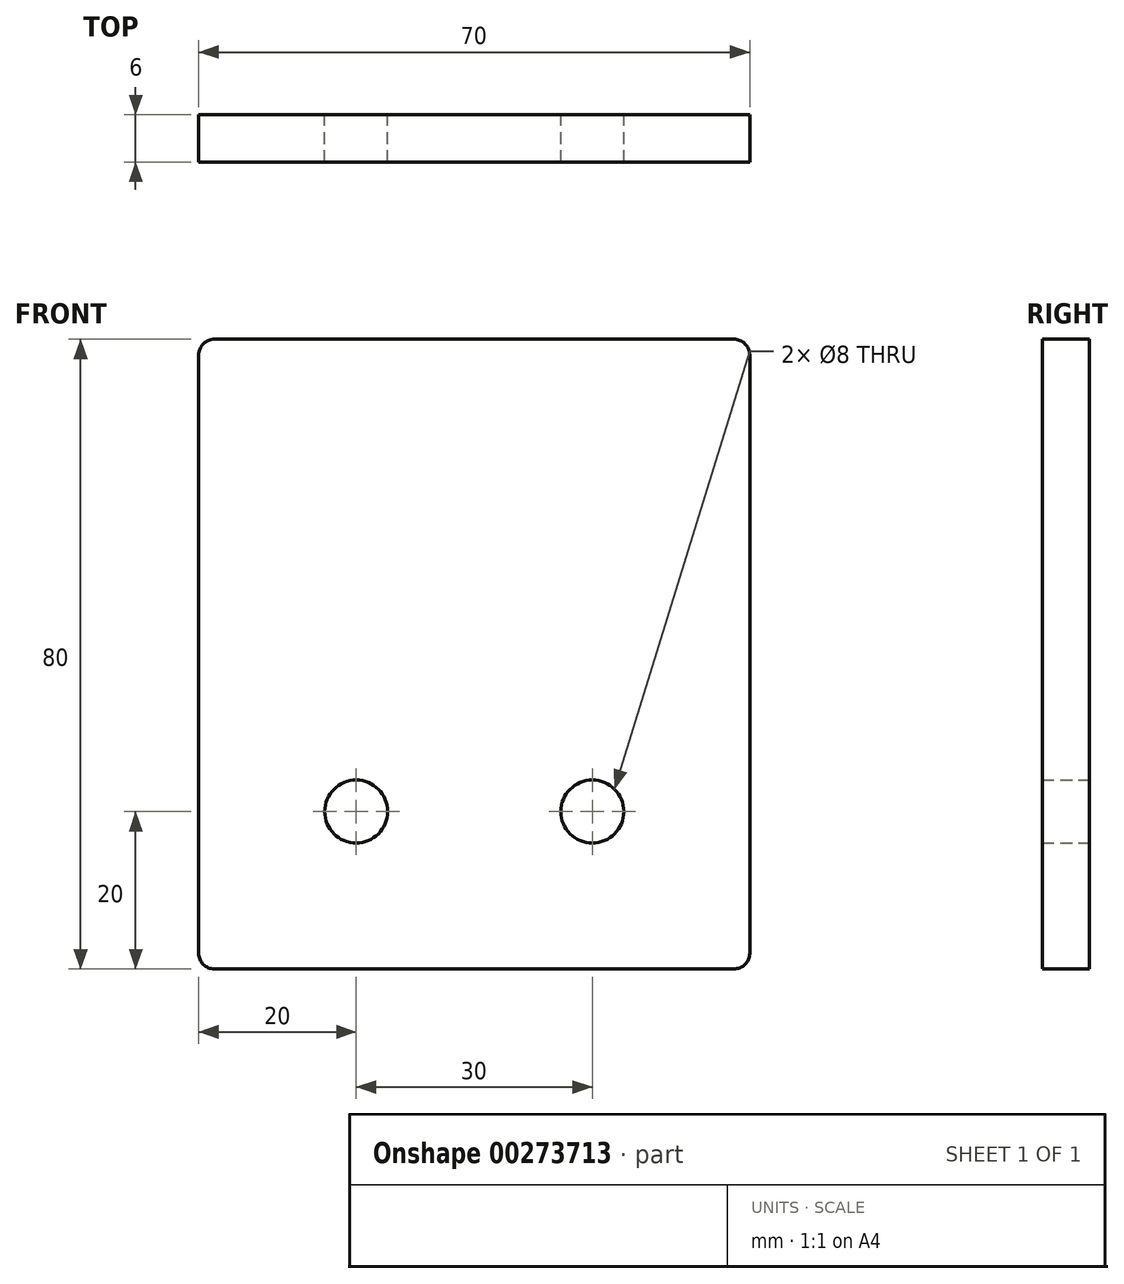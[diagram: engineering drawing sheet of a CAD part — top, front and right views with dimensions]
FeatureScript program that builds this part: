
annotation { "Feature Type Name" : "Feature", "Feature Type Description" : "" }
export const myFeature = defineFeature(function(context is Context, id is Id, definition is map)
    precondition{}
    {
        {
            var Q0;
            Q0=qCreatedBy(makeId("Front.planeOp"),FACE);
            var sketch = newSketch(context, id + "F0", { "sketchPlane" : qUnion([Q0])});
            skLineSegment(sketch, "E0.bottom", {"start": v(33, 40) * mm, "end": v(-33, 40) * mm});
            skLineSegment(sketch, "E0.top", {"start": v(33, -40) * mm, "end": v(-33, -40) * mm});
            skLineSegment(sketch, "E0.left", {"start": v(35, 38) * mm, "end": v(35, -38) * mm});
            skLineSegment(sketch, "E0.right", {"start": v(-35, 38) * mm, "end": v(-35, -38) * mm});
            skPoint(sketch, "E0.middle", {"position": v(0, 0) * mm});
            skPoint(sketch, "E1.visualSharp", {"position": v(-35, 40) * mm});
            skArc(sketch, "E1.filletArc", {"start": v(-33, 40) * mm, "mid": v(-34.41, 39.41) * mm, "end": v(-35, 38) * mm});
            skPoint(sketch, "E2.visualSharp", {"position": v(35, 40) * mm});
            skArc(sketch, "E2.filletArc", {"start": v(35, 38) * mm, "mid": v(34.41, 39.41) * mm, "end": v(33, 40) * mm});
            skPoint(sketch, "E3.visualSharp", {"position": v(35, -40) * mm});
            skArc(sketch, "E3.filletArc", {"start": v(33, -40) * mm, "mid": v(34.41, -39.41) * mm, "end": v(35, -38) * mm});
            skPoint(sketch, "E4.visualSharp", {"position": v(-35, -40) * mm});
            skArc(sketch, "E4.filletArc", {"start": v(-35, -38) * mm, "mid": v(-34.41, -39.41) * mm, "end": v(-33, -40) * mm});
            skPoint(sketch, "E5", {"position": v(-15, -20) * mm});
            skPoint(sketch, "E6", {"position": v(15, -20) * mm});
            skCircle(sketch, "E7", {"center": v(-15, -20) * mm, "radius": 4 * mm});
            skCircle(sketch, "E8", {"center": v(15, -20) * mm, "radius": 4 * mm});
            skSolve(sketch);
        }
        {
            var Q0;
            Q0=makeQuery(id+"F0.imprint","IMPRINT",FACE,{"disambiguationData":[TD([[makeQuery(id+"F0.imprint","IMPRINT",EDGE,{"derivedFrom":sQuery(id+"F0.wireOp",EDGE,"E0.bottom")}),1.0]])]});
            extrude(context, id + "F1", {"entities" : qUnion([Q0]), "depth" : 6 * mm});
        }
    });
